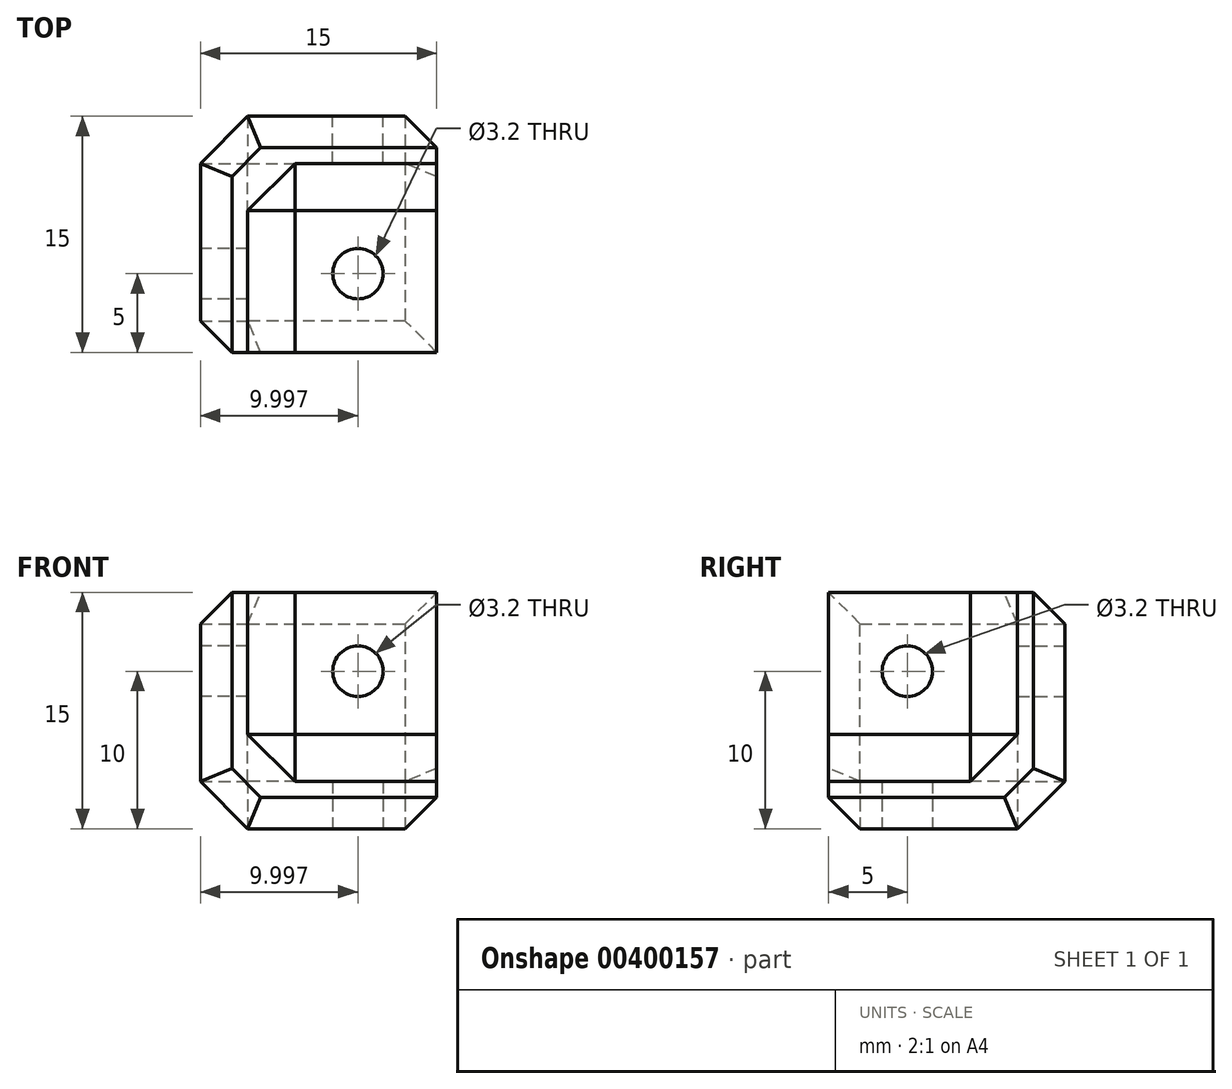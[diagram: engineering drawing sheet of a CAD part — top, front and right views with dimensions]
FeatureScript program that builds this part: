
annotation { "Feature Type Name" : "Feature", "Feature Type Description" : "" }
export const myFeature = defineFeature(function(context is Context, id is Id, definition is map)
    precondition{}
    {
        {
            var Q0;
            Q0=qCreatedBy(makeId("Top.planeOp"),FACE);
            var sketch = newSketch(context, id + "F0", { "sketchPlane" : qUnion([Q0])});
            skLineSegment(sketch, "E0.bottom", {"start": v(-55.5, 0.14) * mm, "end": v(-40.5, 0.14) * mm});
            skLineSegment(sketch, "E0.top", {"start": v(-55.5, -14.86) * mm, "end": v(-40.5, -14.86) * mm});
            skLineSegment(sketch, "E0.left", {"start": v(-55.5, 0.14) * mm, "end": v(-55.5, -14.86) * mm});
            skLineSegment(sketch, "E0.right", {"start": v(-40.5, 0.14) * mm, "end": v(-40.5, -14.86) * mm});
            skLineSegment(sketch, "E1", {"start": v(-52.5, -14.86) * mm, "end": v(-52.5, -2.86) * mm});
            skLineSegment(sketch, "E2", {"start": v(-52.5, -2.86) * mm, "end": v(-40.5, -2.86) * mm});
            skCircle(sketch, "E3", {"center": v(-45.5, -9.86) * mm, "radius": 1.6 * mm});
            skSolve(sketch);
        }
        {
            var Q0;
            {var subQ1=sQuery(id+"F0.wireOp",EDGE,"E0.bottom");Q0=makeQuery(id+"F0.imprint","IMPRINT",FACE,{"disambiguationData":[TD([[makeQuery(id+"F0.imprint","IMPRINT",EDGE,{"derivedFrom":subQ1}),-1.0]])]});}
            var Q1;
            {var subQ3=sQuery(id+"F0.wireOp",EDGE,"E1");Q1=makeQuery(id+"F0.imprint","IMPRINT",FACE,{"disambiguationData":[TD([[makeQuery(id+"F0.imprint","IMPRINT",EDGE,{"derivedFrom":subQ3}),-1.0]])]});}
            extrude(context, id + "F1", {"entities" : qUnion([Q0, Q1]), "depth" : 3 * mm});
        }
        {
            var Q0;
            {var subQ1=sQuery(id+"F0.wireOp",EDGE,"E0.bottom");Q0=makeQuery(id+"F0.imprint","IMPRINT",FACE,{"disambiguationData":[TD([[makeQuery(id+"F0.imprint","IMPRINT",EDGE,{"derivedFrom":subQ1}),-1.0]])]});}
            extrude(context, id + "F2", {"entities" : qUnion([Q0]), "operationType" : NewBodyOperationType.ADD, "depth" : 15 * mm});
        }
        {
            var Q0;
            {var subQ0=sQuery(id+"F0.wireOp",EDGE,"E0.bottom");Q0=makeQuery(id+"F2.boolean.opBoolean","MERGE",FACE,{"derivedFrom":[makeQuery(id+"F1.opExtrude","SWEPT_FACE",FACE,{"disambiguationData":[OSD([subQ0])]}),makeQuery(id+"F2.opExtrude","SWEPT_FACE",FACE,{"disambiguationData":[OSD([subQ0])]})]});}
            var sketch = newSketch(context, id + "F3", { "sketchPlane" : qUnion([Q0])});
            skCircle(sketch, "E4", {"center": v(45.5, 10) * mm, "radius": 1.6 * mm});
            skSolve(sketch);
        }
        {
            var Q0;
            Q0 = qSketchRegion(id + "F3", true);
            extrude(context, id + "F4", {"entities" : qUnion([Q0]), "operationType" : NewBodyOperationType.REMOVE, "oppositeDirection" : true, "depth" : 25 * mm});
        }
        {
            var Q0;
            {var subQ0=sQuery(id+"F0.wireOp",EDGE,"E0.left");Q0=makeQuery(id+"F2.boolean.opBoolean","MERGE",FACE,{"derivedFrom":[makeQuery(id+"F1.opExtrude","SWEPT_FACE",FACE,{"disambiguationData":[OSD([subQ0])]}),makeQuery(id+"F2.opExtrude","SWEPT_FACE",FACE,{"disambiguationData":[OSD([subQ0])]})]});}
            var sketch = newSketch(context, id + "F5", { "sketchPlane" : qUnion([Q0])});
            skCircle(sketch, "E5", {"center": v(9.86, 10) * mm, "radius": 1.6 * mm});
            skSolve(sketch);
        }
        {
            var Q0;
            Q0 = qSketchRegion(id + "F5", true);
            extrude(context, id + "F6", {"entities" : qUnion([Q0]), "operationType" : NewBodyOperationType.REMOVE, "oppositeDirection" : true, "depth" : 25 * mm});
        }
        {
            var Q0;
            Q0=makeQuery(id+"F2.opExtrude","CAP_VERTEX",VERTEX,{"disambiguationData":[OSD([sQuery(id+"F0.wireOp",EDGE,"E0.top"),sQuery(id+"F0.wireOp",EDGE,"E1")])],"isStart":false});
            var Q1;
            Q1=makeQuery(id+"F2.opExtrude","CAP_VERTEX",VERTEX,{"disambiguationData":[OSD([sQuery(id+"F0.wireOp",EDGE,"E0.right"),sQuery(id+"F0.wireOp",EDGE,"E2")])],"isStart":false});
            var Q2;
            Q2=makeQuery(id+"F1.opExtrude","CAP_VERTEX",VERTEX,{"disambiguationData":[OSD([sQuery(id+"F0.wireOp",EDGE,"E0.top"),sQuery(id+"F0.wireOp",EDGE,"E0.right")])],"isStart":false});
            cPlane(context, id + "F7", {"entities" : qUnion([Q0, Q1, Q2]), "cplaneType" : CPlaneType.THREE_POINT, "offset" : 25 * mm, "width" : 150 * mm, "height" : 150 * mm});
        }
        {
            var Q0;
            Q0=qCreatedBy(id+"F7.planeOp",FACE);
            var sketch = newSketch(context, id + "F8", { "sketchPlane" : qUnion([Q0])});
            skLineSegment(sketch, "E6", {"start": v(-30.2, 50.45) * mm, "end": v(-13.73, 49.44) * mm});
            skLineSegment(sketch, "E7", {"start": v(-13.73, 49.44) * mm, "end": v(-6.86, 39.33) * mm});
            skLineSegment(sketch, "E8", {"start": v(-6.86, 39.33) * mm, "end": v(-16.3, 24.65) * mm});
            skLineSegment(sketch, "E9", {"start": v(-16.3, 24.65) * mm, "end": v(-31.74, 25.37) * mm});
            skLineSegment(sketch, "E10", {"start": v(-31.74, 25.37) * mm, "end": v(-37.56, 38.88) * mm});
            skLineSegment(sketch, "E11", {"start": v(-37.56, 38.88) * mm, "end": v(-30.2, 50.45) * mm});
            skSolve(sketch);
        }
        {
            var Q0;
            Q0 = qSketchRegion(id + "F8", true);
            extrude(context, id + "F9", {"entities" : qUnion([Q0]), "operationType" : NewBodyOperationType.REMOVE, "oppositeDirection" : true, "depth" : 3 * mm});
        }
        {
            var Q0;
            Q0=makeQuery(id+"F1.opExtrude","CAP_EDGE",EDGE,{"disambiguationData":[OSD([sQuery(id+"F0.wireOp",EDGE,"E0.left")])],"isStart":true});
            var Q1;
            Q1=makeQuery(id+"F1.opExtrude","CAP_EDGE",EDGE,{"disambiguationData":[OSD([sQuery(id+"F0.wireOp",EDGE,"E0.bottom")])],"isStart":true});
            var Q2;
            {var subQ0=sQuery(id+"F0.wireOp",EDGE,"E0.left");var subQ1=sQuery(id+"F0.wireOp",EDGE,"E0.bottom");Q2=makeQuery(id+"F2.boolean.opBoolean","MERGE",EDGE,{"derivedFrom":[makeQuery(id+"F1.opExtrude","SWEPT_EDGE",EDGE,{"disambiguationData":[OSD([subQ1,subQ0])]}),makeQuery(id+"F2.opExtrude","SWEPT_EDGE",EDGE,{"disambiguationData":[OSD([subQ1,subQ0])]})]});}
            var Q3;
            Q3=makeQuery(id+"F2.boolean.opBoolean","INTERSECT",EDGE,{"derivedFrom":[makeQuery(id+"F1.opExtrude","CAP_FACE",FACE,{"disambiguationData":[OSD([sQuery(id+"F0.wireOp",EDGE,"E0.bottom"),sQuery(id+"F0.wireOp",EDGE,"E0.top"),sQuery(id+"F0.wireOp",EDGE,"E0.left"),sQuery(id+"F0.wireOp",EDGE,"E0.right"),sQuery(id+"F0.wireOp",EDGE,"E3")])],"isStart":false}),makeQuery(id+"F2.opExtrude","SWEPT_FACE",FACE,{"disambiguationData":[OSD([sQuery(id+"F0.wireOp",EDGE,"E1")])]})]});
            var Q4;
            Q4=makeQuery(id+"F2.boolean.opBoolean","INTERSECT",EDGE,{"derivedFrom":[makeQuery(id+"F1.opExtrude","CAP_FACE",FACE,{"disambiguationData":[OSD([sQuery(id+"F0.wireOp",EDGE,"E0.bottom"),sQuery(id+"F0.wireOp",EDGE,"E0.top"),sQuery(id+"F0.wireOp",EDGE,"E0.left"),sQuery(id+"F0.wireOp",EDGE,"E0.right"),sQuery(id+"F0.wireOp",EDGE,"E3")])],"isStart":false}),makeQuery(id+"F2.opExtrude","SWEPT_FACE",FACE,{"disambiguationData":[OSD([sQuery(id+"F0.wireOp",EDGE,"E2")])]})]});
            var Q5;
            Q5=makeQuery(id+"F2.opExtrude","SWEPT_EDGE",EDGE,{"disambiguationData":[OSD([sQuery(id+"F0.wireOp",EDGE,"E1"),sQuery(id+"F0.wireOp",EDGE,"E2")])]});
            chamfer(context, id + "F10", {"entities" : qUnion([Q0, Q1, Q2, Q3, Q4, Q5]), "width" : 3 * mm, "tangentPropagation" : true});
        }
        {
            var Q0;
            {var subQ0=sQuery(id+"F0.wireOp",EDGE,"E0.right");var subQ1=sQuery(id+"F0.wireOp",EDGE,"E0.bottom");Q0=makeQuery(id+"F2.boolean.opBoolean","MERGE",EDGE,{"derivedFrom":[makeQuery(id+"F1.opExtrude","SWEPT_EDGE",EDGE,{"disambiguationData":[OSD([subQ1,subQ0])]}),makeQuery(id+"F2.opExtrude","SWEPT_EDGE",EDGE,{"disambiguationData":[OSD([subQ1,subQ0])]})]});}
            var Q1;
            Q1=makeQuery(id+"F1.opExtrude","CAP_EDGE",EDGE,{"disambiguationData":[OSD([sQuery(id+"F0.wireOp",EDGE,"E0.right")])],"isStart":true});
            var Q2;
            Q2=makeQuery(id+"F1.opExtrude","CAP_EDGE",EDGE,{"disambiguationData":[OSD([sQuery(id+"F0.wireOp",EDGE,"E0.top")])],"isStart":true});
            var Q3;
            {var subQ0=sQuery(id+"F0.wireOp",EDGE,"E0.left");var subQ1=sQuery(id+"F0.wireOp",EDGE,"E0.top");Q3=makeQuery(id+"F2.boolean.opBoolean","MERGE",EDGE,{"derivedFrom":[makeQuery(id+"F1.opExtrude","SWEPT_EDGE",EDGE,{"disambiguationData":[OSD([subQ1,subQ0])]}),makeQuery(id+"F2.opExtrude","SWEPT_EDGE",EDGE,{"disambiguationData":[OSD([subQ1,subQ0])]})]});}
            var Q4;
            {var subQ0=sQuery(id+"F0.wireOp",EDGE,"E0.top");Q4=makeQuery(id+"F10.opChamfer","BLEND_EDGE",EDGE,{"blendedFrom":[makeQuery(id+"F1.opExtrude","CAP_EDGE",EDGE,{"disambiguationData":[OSD([sQuery(id+"F0.wireOp",EDGE,"E0.left")])],"isStart":true}),makeQuery(id+"F2.boolean.opBoolean","MERGE",FACE,{"derivedFrom":[makeQuery(id+"F1.opExtrude","SWEPT_FACE",FACE,{"disambiguationData":[OSD([subQ0])]}),makeQuery(id+"F2.opExtrude","SWEPT_FACE",FACE,{"disambiguationData":[OSD([subQ0])]})]})],"blendedInto":[makeQuery(id+"F2.boolean.opBoolean","MERGE",FACE,{"derivedFrom":[makeQuery(id+"F1.opExtrude","SWEPT_FACE",FACE,{"disambiguationData":[OSD([subQ0])]}),makeQuery(id+"F2.opExtrude","SWEPT_FACE",FACE,{"disambiguationData":[OSD([subQ0])]})]})]});}
            var Q5;
            {var subQ0=sQuery(id+"F0.wireOp",EDGE,"E0.left");var subQ1=sQuery(id+"F0.wireOp",EDGE,"E0.bottom");Q5=makeQuery(id+"F10.opChamfer","BLEND_EDGE",EDGE,{"blendedFrom":[makeQuery(id+"F2.boolean.opBoolean","MERGE",EDGE,{"derivedFrom":[makeQuery(id+"F1.opExtrude","SWEPT_EDGE",EDGE,{"disambiguationData":[OSD([subQ1,subQ0])]}),makeQuery(id+"F2.opExtrude","SWEPT_EDGE",EDGE,{"disambiguationData":[OSD([subQ1,subQ0])]})]}),makeQuery(id+"F2.opExtrude","CAP_FACE",FACE,{"disambiguationData":[OSD([subQ1,sQuery(id+"F0.wireOp",EDGE,"E0.top"),subQ0,sQuery(id+"F0.wireOp",EDGE,"E0.right"),sQuery(id+"F0.wireOp",EDGE,"E1"),sQuery(id+"F0.wireOp",EDGE,"E2")])],"isStart":false})],"blendedInto":[makeQuery(id+"F2.opExtrude","CAP_FACE",FACE,{"disambiguationData":[OSD([subQ1,sQuery(id+"F0.wireOp",EDGE,"E0.top"),subQ0,sQuery(id+"F0.wireOp",EDGE,"E0.right"),sQuery(id+"F0.wireOp",EDGE,"E1"),sQuery(id+"F0.wireOp",EDGE,"E2")])],"isStart":false})]});}
            var Q6;
            Q6=makeQuery(id+"F2.opExtrude","CAP_EDGE",EDGE,{"disambiguationData":[OSD([sQuery(id+"F0.wireOp",EDGE,"E0.left")])],"isStart":false});
            var Q7;
            Q7=makeQuery(id+"F2.opExtrude","CAP_EDGE",EDGE,{"disambiguationData":[OSD([sQuery(id+"F0.wireOp",EDGE,"E0.bottom")])],"isStart":false});
            var Q8;
            {var subQ0=sQuery(id+"F0.wireOp",EDGE,"E0.right");Q8=makeQuery(id+"F10.opChamfer","BLEND_EDGE",EDGE,{"blendedFrom":[makeQuery(id+"F1.opExtrude","CAP_EDGE",EDGE,{"disambiguationData":[OSD([sQuery(id+"F0.wireOp",EDGE,"E0.bottom")])],"isStart":true}),makeQuery(id+"F2.boolean.opBoolean","MERGE",FACE,{"derivedFrom":[makeQuery(id+"F1.opExtrude","SWEPT_FACE",FACE,{"disambiguationData":[OSD([subQ0])]}),makeQuery(id+"F2.opExtrude","SWEPT_FACE",FACE,{"disambiguationData":[OSD([subQ0])]})]})],"blendedInto":[makeQuery(id+"F2.boolean.opBoolean","MERGE",FACE,{"derivedFrom":[makeQuery(id+"F1.opExtrude","SWEPT_FACE",FACE,{"disambiguationData":[OSD([subQ0])]}),makeQuery(id+"F2.opExtrude","SWEPT_FACE",FACE,{"disambiguationData":[OSD([subQ0])]})]})]});}
            chamfer(context, id + "F11", {"entities" : qUnion([Q0, Q1, Q2, Q3, Q4, Q5, Q6, Q7, Q8]), "width" : 2 * mm, "tangentPropagation" : true});
        }
    });
